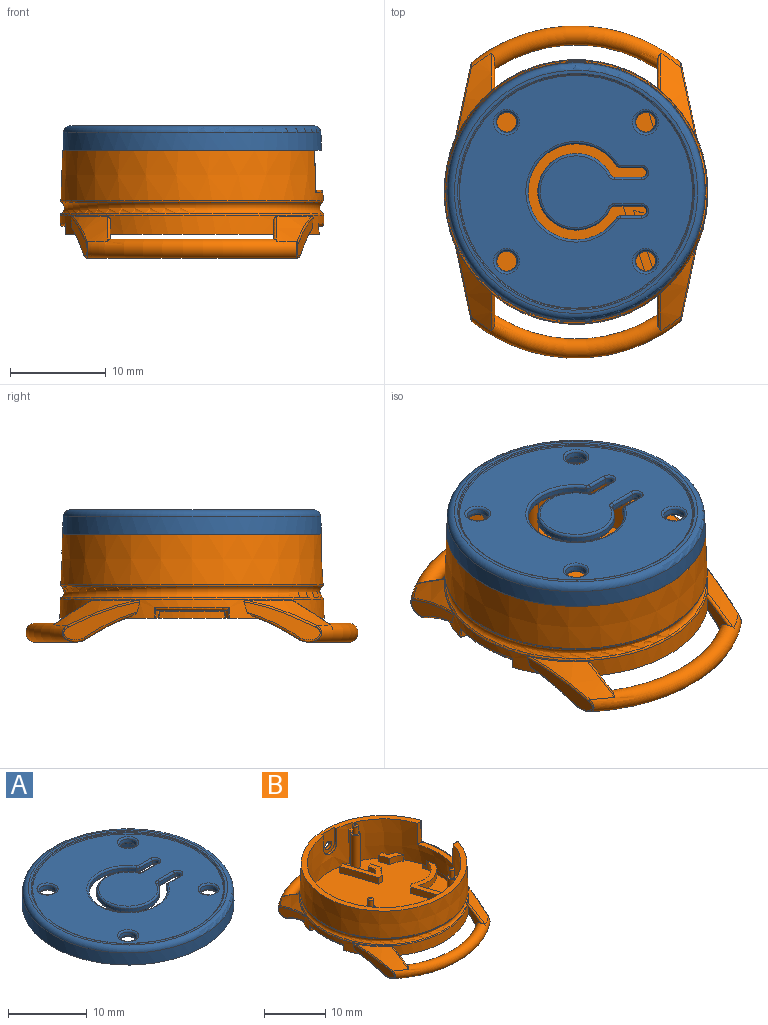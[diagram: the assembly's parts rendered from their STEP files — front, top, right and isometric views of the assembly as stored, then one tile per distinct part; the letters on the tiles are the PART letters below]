
ASSEMBLY  parts=2 mates=1
PART A: 83 faces, bbox 29.1x29.1x2.6 mm
  f0: plane 24.95x24.95mm, normal (0,0,-1), area 402.1mm2, adj f1,f2,f3,f24,f25,f26,f27,f28
  f1: cone r=12.5mm half-angle=1deg, axis (0,0,-1), area 38.1mm2, adj f0,f7,f73,f76
  f2: cone r=12.5mm half-angle=1deg, axis (0,0,-1), area 33.4mm2, adj f0,f7,f65,f69
  f3: cone r=12.5mm half-angle=1deg, axis (0,0,-1), area 22.8mm2, adj f0,f7,f67,f80
  f4: plane 24.3x24.3mm, normal (0,0,1), area 394.8mm2, adj f11,f36,f37,f38,f39,f40,f41,f42
  f5: cone r=13.5mm half-angle=2deg, axis (0,0,-1), area 154.6mm2, adj f7,f8
  f6: plane 25.37x25.37mm, normal (0,0,1), area 26.5mm2, adj f8,f10
  f7: plane 27x27mm, normal (0,0,-1), area 91.9mm2, adj f1,f2,f3,f5,f64,f65,f66,f67
  f8: torus R=12.69mm, axis (0,0,1), area 95.2mm2, adj f5,f6
  f9: cylinder r=12.25mm len=24.5mm, axis (0,0,1), area 3.8mm2, adj f10,f11
  f10: torus R=12.35mm, axis (0,0,1), area 12.1mm2, adj f6,f9
  f11: torus R=12.15mm, axis (0,0,1), area 12.1mm2, adj f4,f9
  f12: cylinder r=0.5mm len=0.5mm, axis (0,0,1), area 0.2mm2, adj f13,f23,f25,f37
  f13: cylinder r=5mm len=10mm, axis (0,0,1), area 12.8mm2, adj f12,f14,f24,f36
  f14: cylinder r=0.5mm len=0.5mm, axis (0,0,1), area 0.2mm2, adj f13,f15,f26,f38
  f15: plane 2.22x0.5mm, normal (0,1,0), area 1.1mm2, adj f14,f16,f28,f40
  f16: cylinder r=0.5mm len=1mm, axis (0,0,1), area 0.8mm2, adj f15,f17,f30,f42
  f17: plane 2.8x0.5mm, normal (0,-1,0), area 1.4mm2, adj f16,f18,f32,f44
  f18: cylinder r=0.5mm len=0.5mm, axis (0,0,1), area 0.3mm2, adj f17,f19,f34,f46
  f19: cylinder r=4mm len=8mm, axis (0,0,1), area 10.7mm2, adj f18,f20,f35,f47
  f20: cylinder r=0.5mm len=0.5mm, axis (0,0,1), area 0.3mm2, adj f19,f21,f33,f45
  f21: plane 2.8x0.5mm, normal (0,1,0), area 1.4mm2, adj f20,f22,f31,f43
  f22: cylinder r=0.5mm len=1mm, axis (0,0,1), area 0.8mm2, adj f21,f23,f29,f41
  f23: plane 2.22x0.5mm, normal (0,-1,0), area 1.1mm2, adj f12,f22,f27,f39
  f24: torus R=5.25mm, axis (0,0,1), area 10.3mm2, adj f0,f13,f25,f26
  f25: torus R=0.25mm, axis (0,0,1), area 0.2mm2, adj f0,f12,f24,f27
  f26: torus R=0.25mm, axis (0,0,1), area 0.2mm2, adj f0,f14,f24,f28
  f27: cylinder r=0.25mm len=2.22mm, axis (-1,0,0), area 0.9mm2, adj f0,f23,f25,f29
  f28: cylinder r=0.25mm len=2.22mm, axis (1,0,0), area 0.9mm2, adj f0,f15,f26,f30
  f29: torus R=0.75mm, axis (0,0,1), area 0.7mm2, adj f0,f22,f27,f31
  f30: torus R=0.75mm, axis (0,0,1), area 0.7mm2, adj f0,f16,f28,f32
  f31: cylinder r=0.25mm len=2.8mm, axis (1,0,0), area 1.1mm2, adj f0,f21,f29,f33
  f32: cylinder r=0.25mm len=2.8mm, axis (-1,0,0), area 1.1mm2, adj f0,f17,f30,f34
  f33: torus R=0.75mm, axis (0,0,1), area 0.3mm2, adj f0,f20,f31,f35
  f34: torus R=0.75mm, axis (0,0,1), area 0.3mm2, adj f0,f18,f32,f35
  f35: torus R=3.75mm, axis (0,0,1), area 8.2mm2, adj f0,f19,f33,f34
  f36: torus R=5.25mm, axis (0,0,1), area 10.3mm2, adj f4,f13,f37,f38
  f37: torus R=0.25mm, axis (0,0,1), area 0.2mm2, adj f4,f12,f36,f39
  f38: torus R=0.25mm, axis (0,0,1), area 0.2mm2, adj f4,f14,f36,f40
  f39: cylinder r=0.25mm len=2.22mm, axis (1,0,0), area 0.9mm2, adj f4,f23,f37,f41
  f40: cylinder r=0.25mm len=2.22mm, axis (-1,0,0), area 0.9mm2, adj f4,f15,f38,f42
  f41: torus R=0.75mm, axis (0,0,1), area 0.7mm2, adj f4,f22,f39,f43
  f42: torus R=0.75mm, axis (0,0,1), area 0.7mm2, adj f4,f16,f40,f44
  f43: cylinder r=0.25mm len=2.8mm, axis (-1,0,0), area 1.1mm2, adj f4,f21,f41,f45
  f44: cylinder r=0.25mm len=2.8mm, axis (1,0,0), area 1.1mm2, adj f4,f17,f42,f46
  f45: torus R=0.75mm, axis (0,0,1), area 0.3mm2, adj f4,f20,f43,f47
  f46: torus R=0.75mm, axis (0,0,1), area 0.3mm2, adj f4,f18,f44,f47
  f47: torus R=3.75mm, axis (0,0,1), area 8.2mm2, adj f4,f19,f45,f46
  f48: cone r=1.5mm half-angle=20deg, axis (0,0,1), area 7.1mm2, adj f50,f51
  f49: plane 2.06x2.06mm, normal (0,0,-1), area 3.3mm2, adj f51
  f50: torus R=1.61mm, axis (0,0,1), area 1.8mm2, adj f0,f48
  f51: torus R=1.03mm, axis (0,0,-1), area 1.3mm2, adj f48,f49
  f52: cone r=1.12mm half-angle=8deg, axis (0,0,1), area 3.4mm2, adj f59,f63
  f53: cone r=1.12mm half-angle=8deg, axis (0,0,1), area 3.4mm2, adj f58,f62
  f54: cone r=1.12mm half-angle=8deg, axis (0,0,1), area 3.4mm2, adj f57,f61
  f55: cone r=1.12mm half-angle=8deg, axis (0,0,1), area 3.4mm2, adj f56,f60
  f56: torus R=1.27mm, axis (0,0,1), area 3mm2, adj f0,f55
  f57: torus R=1.27mm, axis (0,0,1), area 3mm2, adj f0,f54
  f58: torus R=1.27mm, axis (0,0,1), area 3mm2, adj f0,f53,f78
  f59: torus R=1.27mm, axis (0,0,1), area 3mm2, adj f0,f52
  f60: torus R=1.34mm, axis (0,0,1), area 2.7mm2, adj f4,f55
  f61: torus R=1.34mm, axis (0,0,1), area 2.7mm2, adj f4,f54
  f62: torus R=1.34mm, axis (0,0,1), area 2.7mm2, adj f4,f53
  f63: torus R=1.34mm, axis (0,0,1), area 2.7mm2, adj f4,f52
  f64: cylinder r=1mm len=1.84mm, axis (0,0,1), area 4.1mm2, adj f0,f7,f65,f67
  f65: plane 1.3x1mm, normal (0.84,0.55,0), area 1.5mm2, adj f0,f2,f7,f64
  f66: cylinder r=0.48mm len=1.3mm, axis (0,0,1), area 3.9mm2, adj f7,f68
  f67: plane 1.3x1mm, normal (-0.84,-0.55,0), area 1.5mm2, adj f0,f3,f7,f64
  f68: plane 0.96x0.96mm, normal (0,0,-1), area 0.7mm2, adj f66
  f69: plane 1.4x1.3mm, normal (0.94,-0.34,0), area 1.9mm2, adj f0,f2,f7,f70
  f70: cylinder r=1mm len=1.3mm, axis (0,0,1), area 0.2mm2, adj f0,f7,f69,f71
  f71: plane 1.75x1.3mm, normal (0,-1,0), area 2.3mm2, adj f0,f7,f70,f72
  f72: cylinder r=1mm len=1.3mm, axis (0,0,1), area 1.1mm2, adj f0,f7,f71,f73
  f73: plane 1.4x1.3mm, normal (-0.94,0.34,0), area 1.9mm2, adj f0,f1,f7,f72
  f74: cylinder r=0.48mm len=1.3mm, axis (0,0,1), area 3.9mm2, adj f7,f75
  f75: plane 0.96x0.96mm, normal (0,0,-1), area 0.7mm2, adj f74
  f76: plane 1.3x1.16mm, normal (-0.55,0.83,0), area 1.8mm2, adj f0,f1,f7,f77
  f77: cylinder r=1mm len=1.55mm, axis (0,0,1), area 3.4mm2, adj f0,f7,f76,f78
  f78: cylinder r=1.27mm len=1.3mm, axis (0,0,1), area 0.1mm2, adj f7,f58,f77,f79
  f79: cylinder r=1mm len=1.3mm, axis (0,0,1), area 0.5mm2, adj f0,f7,f78,f80
  f80: plane 1.3x1.16mm, normal (0.55,-0.83,0), area 1.8mm2, adj f0,f3,f7,f79
  f81: cylinder r=0.48mm len=1.3mm, axis (0,0,1), area 3.9mm2, adj f7,f82
  f82: plane 0.96x0.96mm, normal (0,0,-1), area 0.7mm2, adj f81
PART B: 130 faces, bbox 30.8x37.6x41 mm
  f0: plane 27.64x26.52mm, normal (0,0,-1), area 580.9mm2, adj f1,f78,f79,f87,f88,f90,f91,f95
  f1: cone r=13.5mm half-angle=2deg, axis (0,0,-1), area 105.7mm2, adj f0,f71,f72,f73,f74,f75,f77,f80
  f2: cone r=13.5mm half-angle=2deg, axis (0,0,-1), area 406.9mm2, adj f6,f60,f61,f62,f64,f70
  f3: cylinder r=0.75mm len=6.7mm, axis (0,0,-1), area 21.5mm2, adj f4,f11,f12,f13,f45,f47,f50,f56
  f4: plane 24.73x24.73mm, normal (0,0,1), area 439.1mm2, adj f3,f5,f8,f9,f10,f12,f13,f14
  f5: cone r=12.5mm half-angle=1deg, axis (0,0,1), area 541mm2, adj f4,f6,f7,f8,f9,f11,f12,f13
  f6: plane 27.02x26.29mm, normal (0,0,1), area 72.2mm2, adj f2,f5,f58,f59,f60,f61,f66,f67
  f7: plane 2.32x1.7mm, normal (0,0,1), area 1.9mm2, adj f5,f8,f9,f10,f22
  f8: plane 6.7x0.86mm, normal (-0.94,0.34,0), area 5.8mm2, adj f4,f5,f7,f10
  f9: plane 6.7x0.86mm, normal (0.94,-0.34,0), area 5.8mm2, adj f4,f5,f7,f10
  f10: cylinder r=0.75mm len=6.7mm, axis (0,0,-1), area 24.8mm2, adj f4,f7,f8,f9
  f11: plane 2.01x1.8mm, normal (0,0,1), area 1.7mm2, adj f3,f5,f12,f13,f20
  f12: plane 6.7x0.52mm, normal (-0.84,-0.55,0), area 3.7mm2, adj f3,f4,f5,f11
  f13: plane 6.7x0.52mm, normal (0.84,0.55,0), area 3.7mm2, adj f3,f4,f5,f11
  f14: plane 6.7x0.68mm, normal (0.55,-0.83,0), area 5.1mm2, adj f4,f5,f16,f17
  f15: plane 6.7x0.68mm, normal (-0.55,0.83,0), area 5.1mm2, adj f4,f5,f16,f17
  f16: plane 2.18x1.92mm, normal (0,0,1), area 1.9mm2, adj f5,f14,f15,f17,f18
  f17: cylinder r=0.75mm len=6.7mm, axis (0,0,-1), area 24.8mm2, adj f4,f14,f15,f16
  f18: cylinder r=0.43mm len=1.52mm, axis (0,0,-1), area 4.1mm2, adj f16,f24
  f19: plane 0.36x0.36mm, normal (0,0,1), area 0.1mm2, adj f24
  f20: cylinder r=0.43mm len=1.52mm, axis (0,0,-1), area 4.1mm2, adj f11,f26
  f21: plane 0.36x0.36mm, normal (0,0,1), area 0.1mm2, adj f26
  f22: cylinder r=0.43mm len=1.52mm, axis (0,0,-1), area 4.1mm2, adj f7,f25
  f23: plane 0.36x0.36mm, normal (0,0,1), area 0.1mm2, adj f25
  f24: torus R=0.18mm, axis (0,0,1), area 0.8mm2, adj f18,f19
  f25: torus R=0.18mm, axis (0,0,1), area 0.8mm2, adj f22,f23
  f26: torus R=0.18mm, axis (0,0,1), area 0.8mm2, adj f20,f21
  f27: cylinder r=4.1mm len=2.39mm, axis (0,0,-1), area 3.3mm2, adj f4,f28,f32,f33
  f28: plane 1.32x1.25mm, normal (0.96,0.28,0), area 1.7mm2, adj f4,f27,f29,f33
  f29: cylinder r=5mm len=1.31mm, axis (0,0,-1), area 1.7mm2, adj f4,f28,f30,f33
  f30: plane 1.25x1.25mm, normal (0.96,0.28,0), area 1.6mm2, adj f4,f29,f31,f33
  f31: plane 1.25x0.86mm, normal (-0.28,0.96,0), area 1.1mm2, adj f4,f30,f32,f33
  f32: plane 1.81x1.25mm, normal (-0.96,-0.28,0), area 2.4mm2, adj f4,f27,f31,f33
  f33: plane 3.01x2.92mm, normal (0,0,1), area 3.2mm2, adj f27,f28,f29,f30,f31,f32
  f34: plane 1.81x1.25mm, normal (0.96,0.28,0), area 2.4mm2, adj f4,f35,f42,f43
  f35: plane 1.25x0.86mm, normal (-0.28,0.96,0), area 1.1mm2, adj f4,f34,f36,f43
  f36: plane 1.25x1.25mm, normal (-0.96,-0.28,0), area 1.6mm2, adj f4,f35,f37,f43
  f37: cylinder r=5mm len=1.25mm, axis (0,0,-1), area 1.6mm2, adj f4,f36,f38,f43
  f38: plane 5.8x1.92mm, normal (0.95,0.31,0), area 7.6mm2, adj f4,f37,f39,f43
  f39: plane 1.25x0.85mm, normal (-0.31,0.95,0), area 1.1mm2, adj f4,f38,f40,f43
  f40: plane 6.72x2.22mm, normal (-0.95,-0.31,0), area 8.8mm2, adj f4,f39,f41,f43
  f41: plane 1.25x0.95mm, normal (0,-1,0), area 1.2mm2, adj f4,f40,f42,f43
  f42: cylinder r=4.1mm len=1.85mm, axis (0,0,-1), area 3mm2, adj f4,f34,f41,f43
  f43: plane 7x4.6mm, normal (0,0,1), area 9.5mm2, adj f34,f35,f36,f37,f38,f39,f40,f41
  f44: plane 1.25x0.85mm, normal (-0.95,-0.31,0), area 1.1mm2, adj f4,f45,f46,f47
  f45: plane 7.02x2.32mm, normal (0.31,-0.95,0), area 9.2mm2, adj f3,f4,f44,f47
  f46: plane 8.96x2.96mm, normal (-0.31,0.95,0), area 11.8mm2, adj f4,f44,f47,f49,f56
  f47: plane 7.71x3.4mm, normal (0,0,1), area 6.8mm2, adj f3,f44,f45,f46
  f48: plane 1.25x0.76mm, normal (-0.6,0.8,0), area 1.2mm2, adj f4,f49,f55,f56
  f49: plane 7.05x2.33mm, normal (-0.95,-0.31,0), area 9.3mm2, adj f4,f46,f48,f56
  f50: plane 1.25x0.54mm, normal (0.31,-0.95,0), area 0.7mm2, adj f3,f4,f51,f56
  f51: plane 1.25x1.14mm, normal (0.89,-0.46,0), area 1.6mm2, adj f4,f50,f52,f56
  f52: plane 6.13x2.03mm, normal (0.95,0.31,0), area 8.1mm2, adj f4,f51,f53,f56
  f53: cylinder r=5mm len=6.29mm, axis (0,0,-1), area 9.3mm2, adj f4,f52,f54,f56
  f54: plane 1.53x1.25mm, normal (0.96,0.28,0), area 2mm2, adj f4,f53,f55,f56
  f55: cylinder r=4.1mm len=6.24mm, axis (0,0,-1), area 10.1mm2, adj f4,f48,f54,f56
  f56: plane 11.45x7.45mm, normal (0,0,1), area 14.8mm2, adj f3,f46,f48,f49,f50,f51,f52,f53
  f57: plane 8.18x1.67mm, normal (0,0,1), area 8.1mm2, adj f5,f58,f59,f60,f61,f62
  f58: plane 4.17x0.94mm, normal (0,-1,0), area 3.4mm2, adj f5,f6,f57,f60
  f59: plane 4.17x0.94mm, normal (0,1,0), area 3.4mm2, adj f5,f6,f57,f61
  f60: bspline ~34.32x1.61mm, area 2mm2, adj f2,f6,f57,f58,f62
  f61: bspline ~34.32x1.61mm, area 2mm2, adj f2,f6,f57,f59,f62
  f62: torus R=13.4mm, axis (0,0,1), area 3.3mm2, adj f2,f57,f60,f61
  f63: cylinder r=0.75mm len=1.5mm, axis (0,-1,0), area 2.4mm2, adj f64,f68
  f64: bspline ~2.04x2mm, area 2.1mm2, adj f2,f63
  f65: cylinder r=1.5mm len=3mm, axis (0,-1,0), area 2.3mm2, adj f5,f66,f67,f68
  f66: plane 2.87x0.49mm, normal (-1,0,0), area 1.3mm2, adj f5,f6,f65,f68
  f67: plane 2.87x0.49mm, normal (1,0,0), area 1.3mm2, adj f5,f6,f65,f68
  f68: plane 4.37x3mm, normal (0,-1,0), area 10.4mm2, adj f6,f63,f65,f66,f67
  f69: torus R=13.98mm, axis (0,0,-1), area 110.1mm2, adj f70,f71
  f70: torus R=13.43mm, axis (0,0,1), area 20.8mm2, adj f2,f69
  f71: torus R=13.49mm, axis (0,0,-1), area 20.8mm2, adj f1,f69
  f72: plane 7.96x3.99mm, normal (-0.98,-0.19,-0.03), area 11.2mm2, adj f1,f107,f108,f109
  f73: plane 7.96x3.99mm, normal (0.98,-0.19,-0.03), area 11.2mm2, adj f1,f104,f105,f106
  f74: plane 3.06x2.95mm, normal (-1,0,0), area 3.5mm2, adj f1,f76,f94,f95
  f75: plane 3.06x2.95mm, normal (1,0,0), area 3.5mm2, adj f1,f76,f96,f97
  f76: torus R=16.35mm, axis (0,0,1), area 132.4mm2, adj f74,f75,f77,f78,f79,f80,f94,f95
  f77: cone r=16.97mm half-angle=51.5deg, axis (0,0,-1), area 18.3mm2, adj f1,f76,f94,f106
  f78: cone r=13.75mm half-angle=40.5deg, axis (0,0,-1), area 11.3mm2, adj f0,f76,f95,f104
  f79: cone r=13.75mm half-angle=40.5deg, axis (0,0,-1), area 11.3mm2, adj f0,f76,f97,f107
  f80: cone r=16.97mm half-angle=51.5deg, axis (0,0,-1), area 18.3mm2, adj f1,f76,f96,f109
  f81: plane 7.96x3.99mm, normal (-0.98,0.19,-0.03), area 11.2mm2, adj f1,f98,f99,f100
  f82: plane 7.96x3.99mm, normal (0.98,0.19,-0.03), area 11.2mm2, adj f1,f101,f102,f103
  f83: plane 3.06x2.95mm, normal (-1,0,0), area 3.5mm2, adj f1,f85,f91,f92
  f84: plane 3.06x2.95mm, normal (1,0,0), area 3.5mm2, adj f1,f85,f90,f93
  f85: torus R=16.35mm, axis (0,0,1), area 132.4mm2, adj f83,f84,f86,f87,f88,f89,f90,f91
  f86: cone r=16.97mm half-angle=51.5deg, axis (0,0,-1), area 18.3mm2, adj f1,f85,f92,f103
  f87: cone r=13.75mm half-angle=40.5deg, axis (0,0,-1), area 11.3mm2, adj f0,f85,f91,f101
  f88: cone r=13.75mm half-angle=40.5deg, axis (0,0,-1), area 11.3mm2, adj f0,f85,f90,f98
  f89: cone r=16.97mm half-angle=51.5deg, axis (0,0,-1), area 18.3mm2, adj f1,f85,f93,f100
  f90: bspline ~4.11x3.93mm, area 0.8mm2, adj f0,f1,f84,f85,f88
  f91: bspline ~4.11x3.93mm, area 0.8mm2, adj f0,f1,f83,f85,f87
  f92: bspline ~8.11x5.49mm, area 2mm2, adj f1,f83,f85,f86
  f93: bspline ~8.11x5.49mm, area 2mm2, adj f1,f84,f85,f89
  f94: bspline ~8.11x5.49mm, area 2mm2, adj f1,f74,f76,f77
  f95: bspline ~4.11x3.93mm, area 0.8mm2, adj f0,f1,f74,f76,f78
  f96: bspline ~8.11x5.49mm, area 2mm2, adj f1,f75,f76,f80
  f97: bspline ~4.11x3.93mm, area 0.8mm2, adj f0,f1,f75,f76,f79
  f98: bspline ~8.91x5.02mm, area 3mm2, adj f0,f1,f81,f88,f99
  f99: bspline ~2.82x1.97mm, area 1.2mm2, adj f81,f85,f98,f100
  f100: bspline ~11.77x4.5mm, area 2mm2, adj f1,f81,f89,f99
  f101: bspline ~8.91x5.02mm, area 3mm2, adj f0,f1,f82,f87,f102
  f102: bspline ~2.75x1.98mm, area 1.2mm2, adj f82,f85,f101,f103
  f103: bspline ~11.77x4.5mm, area 2mm2, adj f1,f82,f86,f102
  f104: bspline ~8.91x5.02mm, area 3mm2, adj f0,f1,f73,f78,f105
  f105: bspline ~2.75x1.98mm, area 1.2mm2, adj f73,f76,f104,f106
  f106: bspline ~11.77x4.5mm, area 2mm2, adj f1,f73,f77,f105
  f107: bspline ~8.91x5.02mm, area 3mm2, adj f0,f1,f72,f79,f108
  f108: bspline ~2.82x1.97mm, area 1.2mm2, adj f72,f76,f107,f109
  f109: bspline ~11.77x4.5mm, area 2mm2, adj f1,f72,f80,f108
  f110: cone r=12.75mm half-angle=5.2deg, axis (0,0,1), area 4.9mm2, adj f0,f124,f125,f126
  f111: plane 0.91x0.85mm, normal (-0.28,-0.96,0), area 0.7mm2, adj f0,f113,f119,f120,f124
  f112: plane 0.91x0.85mm, normal (-0.28,0.96,0), area 0.7mm2, adj f0,f113,f119,f121,f125
  f113: plane 7.45x1.13mm, normal (0,0,-1), area 4.7mm2, adj f111,f112,f119,f124,f125,f126
  f114: cone r=12.75mm half-angle=5.2deg, axis (0,0,1), area 4.9mm2, adj f0,f127,f128,f129
  f115: plane 0.91x0.85mm, normal (0.28,0.96,0), area 0.7mm2, adj f0,f117,f118,f122,f127
  f116: plane 0.91x0.85mm, normal (0.28,-0.96,0), area 0.7mm2, adj f0,f117,f118,f123,f128
  f117: plane 7.45x1.13mm, normal (0,0,-1), area 4.7mm2, adj f115,f116,f118,f127,f128,f129
  f118: torus R=13.52mm, axis (0,0,-1), area 3.1mm2, adj f1,f115,f116,f117,f122,f123
  f119: torus R=13.52mm, axis (0,0,-1), area 3.1mm2, adj f1,f111,f112,f113,f120,f121
  f120: bspline ~35.25x1.28mm, area 0.2mm2, adj f0,f1,f111,f119
  f121: bspline ~35.25x1.28mm, area 0.2mm2, adj f0,f1,f112,f119
  f122: bspline ~35.25x1.28mm, area 0.2mm2, adj f0,f1,f115,f118
  f123: bspline ~35.25x1.28mm, area 0.2mm2, adj f0,f1,f116,f118
  f124: bspline ~10.89x1.09mm, area 0.2mm2, adj f0,f110,f111,f113,f126
  f125: bspline ~10.89x1.09mm, area 0.2mm2, adj f0,f110,f112,f113,f126
  f126: torus R=12.89mm, axis (0,0,-1), area 1.6mm2, adj f110,f113,f124,f125
  f127: bspline ~10.89x1.09mm, area 0.2mm2, adj f0,f114,f115,f117,f129
  f128: bspline ~10.89x1.09mm, area 0.2mm2, adj f0,f114,f116,f117,f129
  f129: torus R=12.89mm, axis (0,0,-1), area 1.6mm2, adj f114,f117,f127,f128
PLACE A t=(0,0,7.76)mm
PLACE B at identity fixed
MATE fastened B.f1 <-> A.f1  axis (0,0,1) through (0,0,7.76)mm
